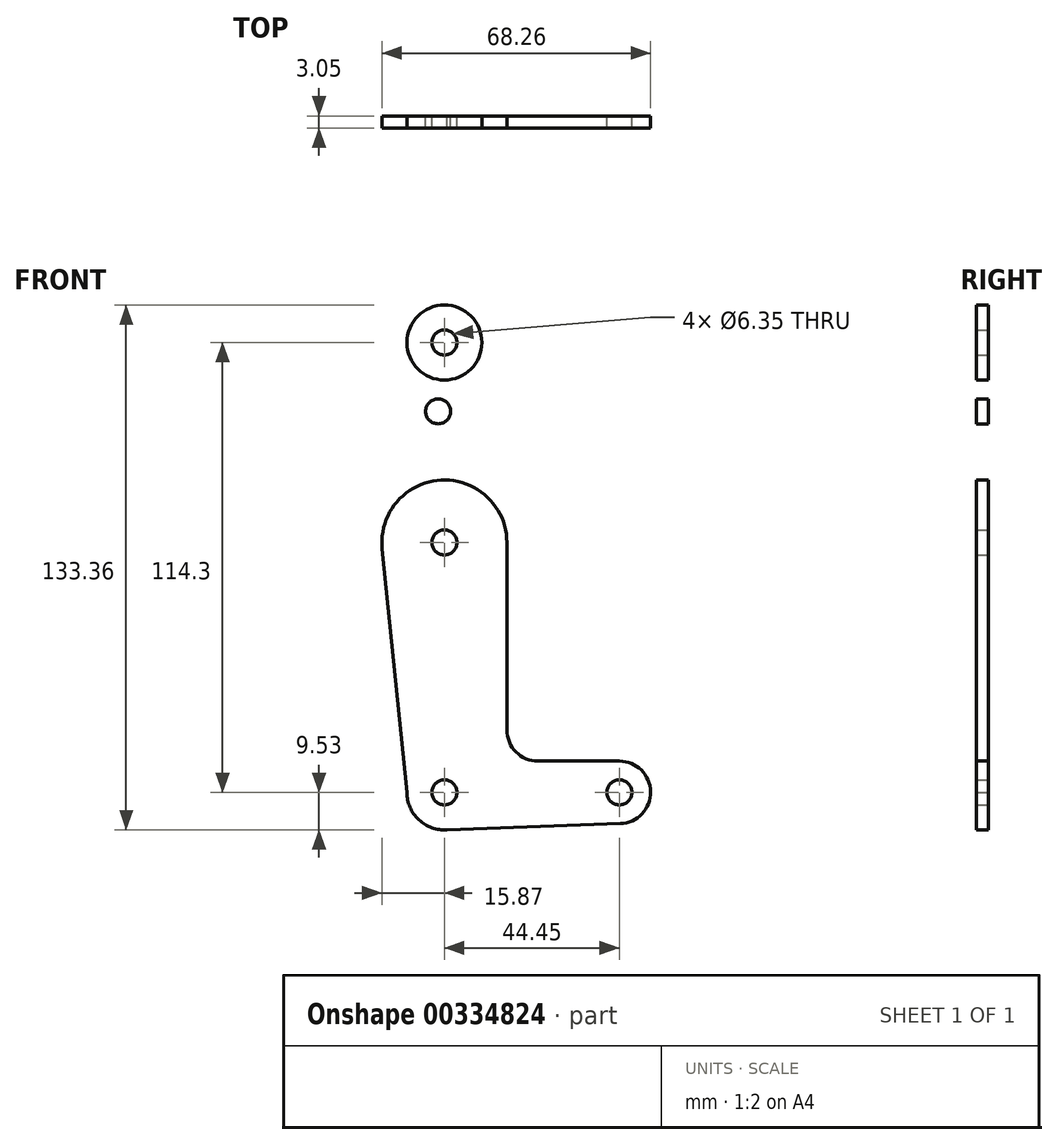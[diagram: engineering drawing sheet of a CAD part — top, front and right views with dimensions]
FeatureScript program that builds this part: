
annotation { "Feature Type Name" : "Feature", "Feature Type Description" : "" }
export const myFeature = defineFeature(function(context is Context, id is Id, definition is map)
    precondition{}
    {
        {
            var Q0;
            Q0=qCreatedBy(makeId("Front.planeOp"),FACE);
            var sketch = newSketch(context, id + "F0", { "sketchPlane" : qUnion([Q0])});
            skLineSegment(sketch, "E0", {"start": v(0, 0) * mm, "end": v(0, 114.3) * mm, "construction": true});
            skLineSegment(sketch, "E1", {"start": v(0, 0) * mm, "end": v(44.45, 0) * mm, "construction": true});
            skCircle(sketch, "E2", {"center": v(0, 114.3) * mm, "radius": 9.53 * mm});
            skCircle(sketch, "E3", {"center": v(0, 63.5) * mm, "radius": 15.88 * mm});
            skCircle(sketch, "E4", {"center": v(0, 0) * mm, "radius": 9.53 * mm});
            skCircle(sketch, "E5", {"center": v(44.45, 0) * mm, "radius": 7.94 * mm});
            skLineSegment(sketch, "E6", {"start": v(-9.53, 114.3) * mm, "end": v(-15.75, 65.5) * mm});
            skLineSegment(sketch, "E7", {"start": v(-9.53, 0) * mm, "end": v(-15.8, 61.9) * mm});
            skLineSegment(sketch, "E8", {"start": v(9.45, 115.5) * mm, "end": v(15.75, 65.5) * mm});
            skLineSegment(sketch, "E9", {"start": v(15.87, 63.5) * mm, "end": v(15.88, 15.89) * mm});
            skLineSegment(sketch, "E10", {"start": v(23.83, 7.94) * mm, "end": v(44.45, 7.94) * mm});
            skLineSegment(sketch, "E11", {"start": v(0, -9.53) * mm, "end": v(44.73, -7.93) * mm});
            skCircle(sketch, "E12", {"center": v(0, 114.3) * mm, "radius": 3.18 * mm});
            skCircle(sketch, "E13", {"center": v(-1.59, 96.81) * mm, "radius": 3.18 * mm});
            skCircle(sketch, "E14", {"center": v(0, 63.5) * mm, "radius": 3.18 * mm});
            skCircle(sketch, "E15", {"center": v(0, 0) * mm, "radius": 3.18 * mm});
            skCircle(sketch, "E16", {"center": v(44.45, 0) * mm, "radius": 3.18 * mm});
            skArc(sketch, "E17.filletArc", {"start": v(15.88, 15.89) * mm, "mid": v(18.2, 10.27) * mm, "end": v(23.83, 7.94) * mm});
            skSolve(sketch);
        }
        {
            var Q0;
            Q0 = qSketchRegion(id + "F0", true);
            extrude(context, id + "F1", {"entities" : qUnion([Q0]), "depth" : 3.05 * mm});
        }
    });
